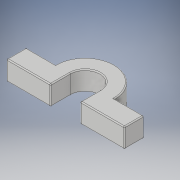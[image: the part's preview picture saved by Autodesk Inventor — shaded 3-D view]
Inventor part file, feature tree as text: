
AUTODESK INVENTOR PART (.ipt)
format: ipt  version: 2019 (Build 230136000, 136)  size: 168,448 bytes
history: native  units: mm
features: extrude x1, fillet x1, sketch x1
ambient origin geometry x8: Origin, YZ Plane, XZ Plane, XY Plane, X Axis, Y Axis, Z Axis, Center Point
bodies: Solid1 (feature_tree)
feature tree (3):
  extrude  "Extrusion1"  Depth=0.5mm
  fillet  "Fillet1"  Radius=10.0mm
  sketch  "Sketch1"  dims[d0=30.0mm d1=15.0mm d5=10.0mm d6=10.0mm d7=15.0mm d9=10.0mm d10=0.0mm d11=30.0mm d12=10.0mm d13=10.0mm d14=0.0mm d15=30.0mm d16=37.5mm d17=0.5mm d18=0.5mm]
